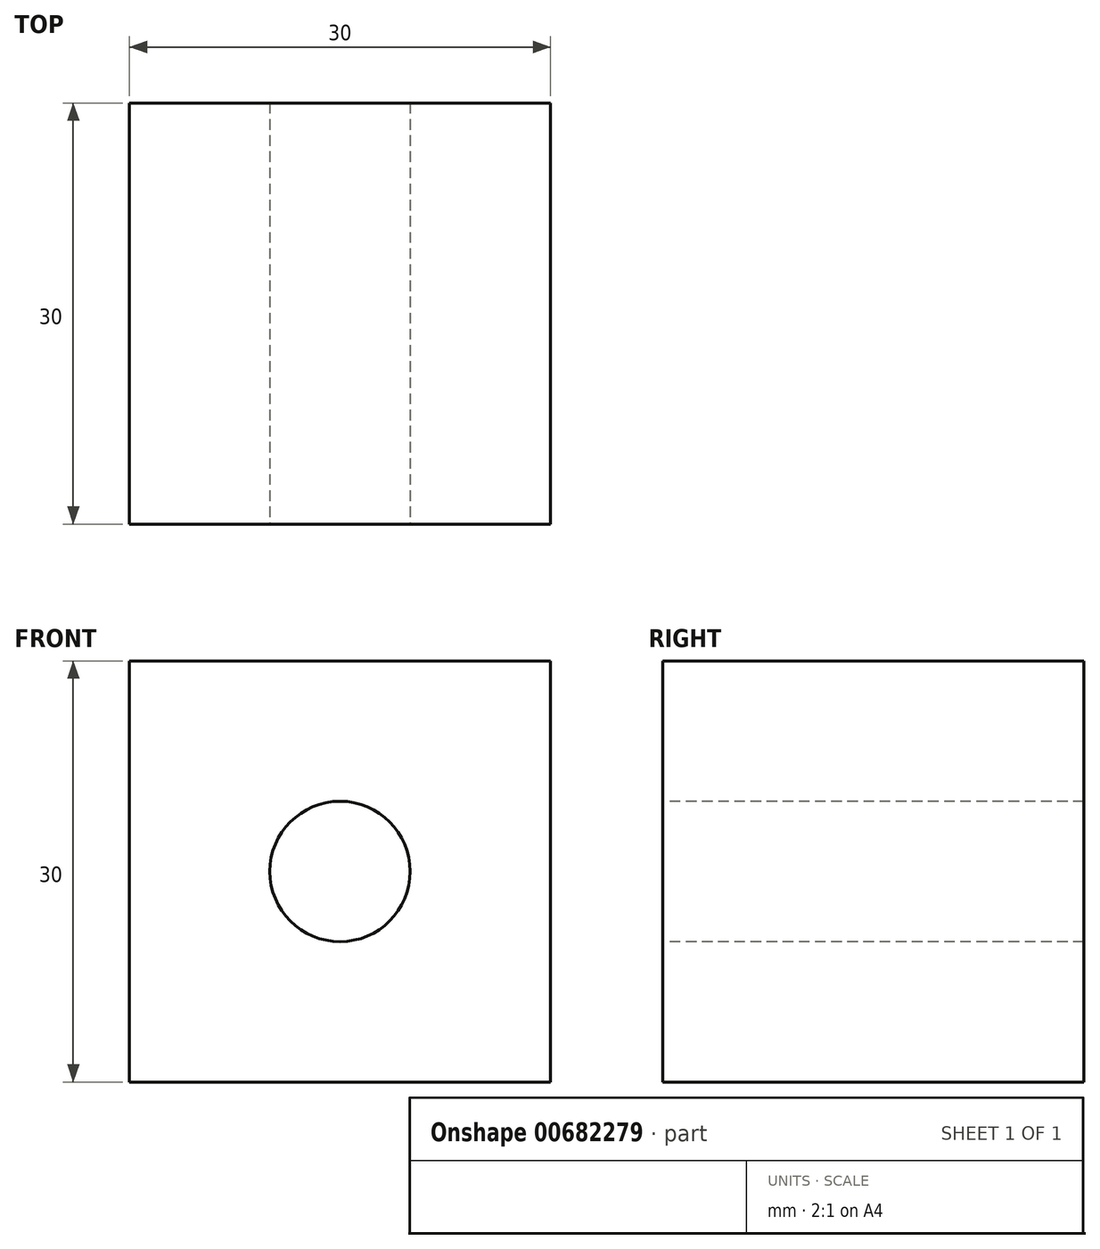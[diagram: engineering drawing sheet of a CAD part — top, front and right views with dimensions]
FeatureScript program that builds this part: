
annotation { "Feature Type Name" : "Feature", "Feature Type Description" : "" }
export const myFeature = defineFeature(function(context is Context, id is Id, definition is map)
    precondition{}
    {
        {
            var Q0;
            Q0=qCreatedBy(makeId("Front.planeOp"),FACE);
            var sketch = newSketch(context, id + "F0", { "sketchPlane" : qUnion([Q0])});
            skLineSegment(sketch, "E0.bottom", {"start": v(15, 15) * mm, "end": v(-15, 15) * mm});
            skLineSegment(sketch, "E0.top", {"start": v(15, -15) * mm, "end": v(-15, -15) * mm});
            skLineSegment(sketch, "E0.left", {"start": v(15, 15) * mm, "end": v(15, -15) * mm});
            skLineSegment(sketch, "E0.right", {"start": v(-15, 15) * mm, "end": v(-15, -15) * mm});
            skPoint(sketch, "E0.middle", {"position": v(0, 0) * mm});
            skSolve(sketch);
        }
        {
            var Q0;
            Q0=makeQuery(id+"F0.imprint","IMPRINT",FACE,{"disambiguationData":[TD([[makeQuery(id+"F0.imprint","IMPRINT",EDGE,{"derivedFrom":sQuery(id+"F0.wireOp",EDGE,"E0.bottom")}),1.0]])]});
            extrude(context, id + "F1", {"entities" : qUnion([Q0]), "depth" : 30 * mm, "offsetDistance" : 25 * mm});
        }
        {
            var Q0;
            Q0=makeQuery(id+"F1.opExtrude","CAP_FACE",FACE,{"disambiguationData":[OSD([sQuery(id+"F0.wireOp",EDGE,"E0.bottom"),sQuery(id+"F0.wireOp",EDGE,"E0.top"),sQuery(id+"F0.wireOp",EDGE,"E0.left"),sQuery(id+"F0.wireOp",EDGE,"E0.right")])],"isStart":false});
            var sketch = newSketch(context, id + "F2", { "sketchPlane" : qUnion([Q0])});
            skPoint(sketch, "E1.centerSnap0", {"position": v(-15, 0) * mm});
            skSolve(sketch);
        }
        {
            var Q0;
            Q0=makeQuery(id+"F2.imprint","IMPRINT",FACE,{"disambiguationData":[TD([[makeQuery(id+"F2.imprint","IMPRINT",EDGE,{"derivedFrom":makeQuery(id+"F1.opExtrude","CAP_EDGE",EDGE,{"disambiguationData":[OSD([sQuery(id+"F0.wireOp",EDGE,"E0.bottom")])],"isStart":false})}),1.0]])]});
            var sketch = newSketch(context, id + "F3", { "sketchPlane" : qUnion([Q0])});
            skCircle(sketch, "E2", {"center": v(0, 0) * mm, "radius": 5 * mm});
            skSolve(sketch);
        }
        {
            var Q0;
            Q0 = qSketchRegion(id + "F3", true);
            extrude(context, id + "F4", {"entities" : qUnion([Q0]), "operationType" : NewBodyOperationType.REMOVE, "oppositeDirection" : true, "depth" : 30 * mm, "offsetDistance" : 25 * mm});
        }
    });
